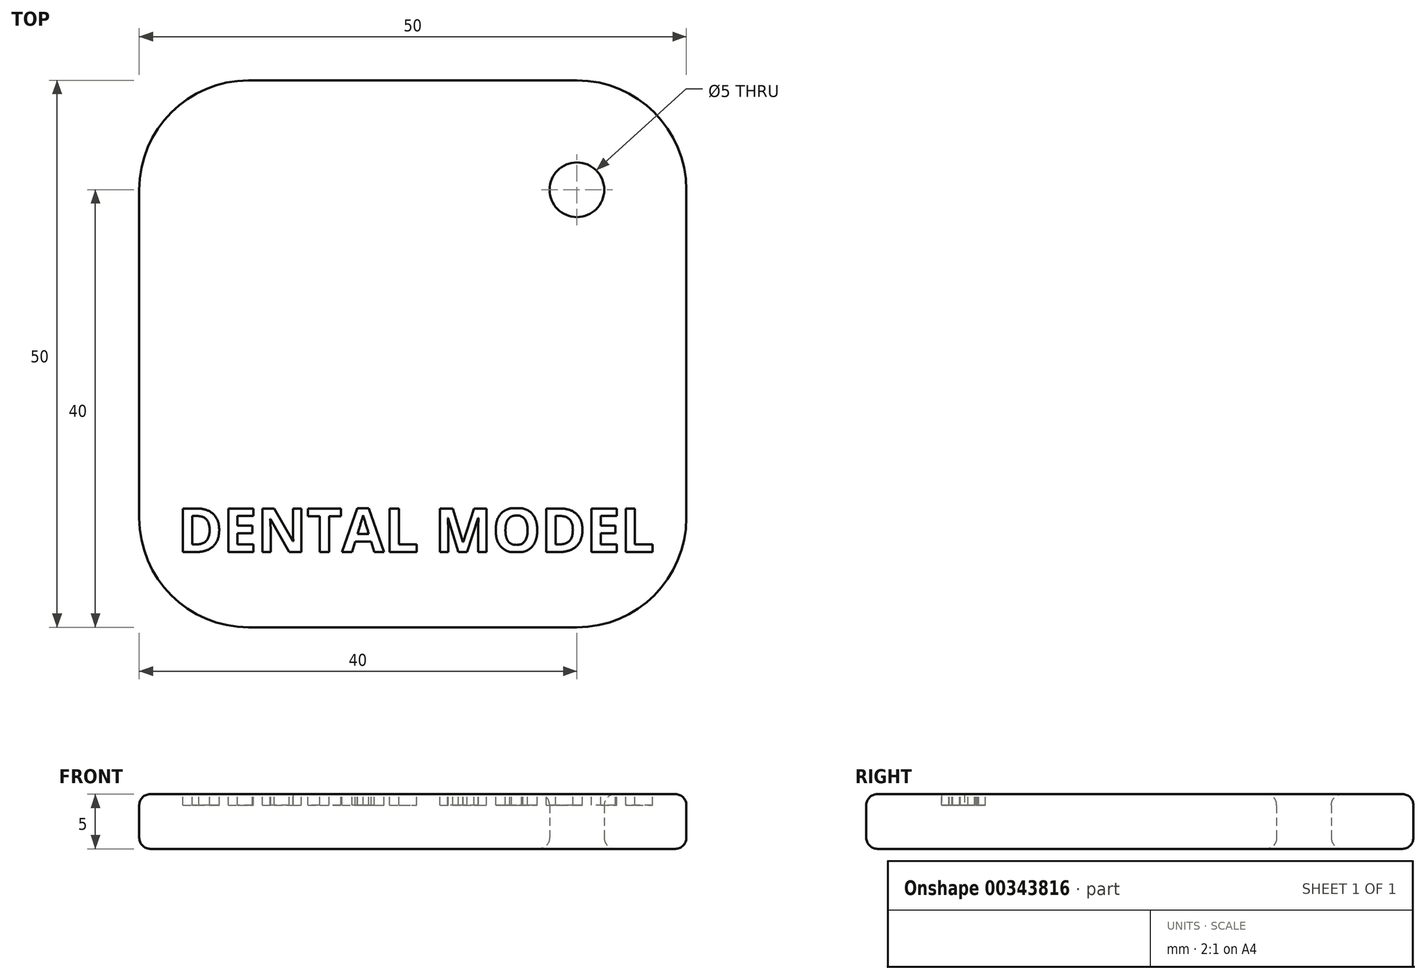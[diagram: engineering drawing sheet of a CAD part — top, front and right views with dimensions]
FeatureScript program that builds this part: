
annotation { "Feature Type Name" : "Feature", "Feature Type Description" : "" }
export const myFeature = defineFeature(function(context is Context, id is Id, definition is map)
    precondition{}
    {
        {
            var Q0;
            Q0=qCreatedBy(makeId("Top.planeOp"),FACE);
            var sketch = newSketch(context, id + "F0", { "sketchPlane" : qUnion([Q0])});
            skLineSegment(sketch, "E0.bottom", {"start": v(10, 0) * mm, "end": v(40, 0) * mm});
            skLineSegment(sketch, "E0.top", {"start": v(10, -50) * mm, "end": v(40, -50) * mm});
            skLineSegment(sketch, "E0.left", {"start": v(0, -10) * mm, "end": v(0, -40) * mm});
            skLineSegment(sketch, "E0.right", {"start": v(50, -10) * mm, "end": v(50, -40) * mm});
            skPoint(sketch, "E1.visualSharp", {"position": v(50, 0) * mm});
            skArc(sketch, "E1.filletArc", {"start": v(50, -10) * mm, "mid": v(47.07, -2.93) * mm, "end": v(40, 0) * mm});
            skPoint(sketch, "E2.visualSharp", {"position": v(50, -50) * mm});
            skArc(sketch, "E2.filletArc", {"start": v(40, -50) * mm, "mid": v(47.07, -47.07) * mm, "end": v(50, -40) * mm});
            skPoint(sketch, "E3.visualSharp", {"position": v(0, -50) * mm});
            skArc(sketch, "E3.filletArc", {"start": v(0, -40) * mm, "mid": v(2.93, -47.07) * mm, "end": v(10, -50) * mm});
            skPoint(sketch, "E4.visualSharp", {"position": v(0, 0) * mm});
            skArc(sketch, "E4.filletArc", {"start": v(10, 0) * mm, "mid": v(2.93, -2.93) * mm, "end": v(0, -10) * mm});
            skCircle(sketch, "E5", {"center": v(40, -10) * mm, "radius": 2.5 * mm});
            skSolve(sketch);
        }
        {
            var Q0;
            Q0=makeQuery(id+"F0.imprint","IMPRINT",FACE,{"disambiguationData":[TD([[makeQuery(id+"F0.imprint","IMPRINT",EDGE,{"derivedFrom":sQuery(id+"F0.wireOp",EDGE,"E0.bottom")}),-1.0]])]});
            extrude(context, id + "F1", {"entities" : qUnion([Q0]), "depth" : 5 * mm, "offsetDistance" : 25 * mm});
        }
        {
            var Q0;
            Q0=makeQuery(id+"F1.opExtrude","CAP_FACE",FACE,{"disambiguationData":[OSD([sQuery(id+"F0.wireOp",EDGE,"E0.bottom"),sQuery(id+"F0.wireOp",EDGE,"E0.top"),sQuery(id+"F0.wireOp",EDGE,"E0.left"),sQuery(id+"F0.wireOp",EDGE,"E0.right"),sQuery(id+"F0.wireOp",EDGE,"E1.filletArc"),sQuery(id+"F0.wireOp",EDGE,"E2.filletArc"),sQuery(id+"F0.wireOp",EDGE,"E3.filletArc"),sQuery(id+"F0.wireOp",EDGE,"E4.filletArc"),sQuery(id+"F0.wireOp",EDGE,"E5")])],"isStart":false});
            var Q1;
            Q1=makeQuery(id+"F1.opExtrude","CAP_FACE",FACE,{"disambiguationData":[OSD([sQuery(id+"F0.wireOp",EDGE,"E0.bottom"),sQuery(id+"F0.wireOp",EDGE,"E0.top"),sQuery(id+"F0.wireOp",EDGE,"E0.left"),sQuery(id+"F0.wireOp",EDGE,"E0.right"),sQuery(id+"F0.wireOp",EDGE,"E1.filletArc"),sQuery(id+"F0.wireOp",EDGE,"E2.filletArc"),sQuery(id+"F0.wireOp",EDGE,"E3.filletArc"),sQuery(id+"F0.wireOp",EDGE,"E4.filletArc"),sQuery(id+"F0.wireOp",EDGE,"E5")])],"isStart":true});
            fillet(context, id + "F2", {"entities" : qUnion([Q0, Q1]), "radius" : 1 * mm, "tangentPropagation" : true, "allowEdgeOverflow" : false});
        }
        {
            var Q0;
            Q0=makeQuery(id+"F1.opExtrude","CAP_FACE",FACE,{"disambiguationData":[OSD([sQuery(id+"F0.wireOp",EDGE,"E0.bottom"),sQuery(id+"F0.wireOp",EDGE,"E0.top"),sQuery(id+"F0.wireOp",EDGE,"E0.left"),sQuery(id+"F0.wireOp",EDGE,"E0.right"),sQuery(id+"F0.wireOp",EDGE,"E1.filletArc"),sQuery(id+"F0.wireOp",EDGE,"E2.filletArc"),sQuery(id+"F0.wireOp",EDGE,"E3.filletArc"),sQuery(id+"F0.wireOp",EDGE,"E4.filletArc"),sQuery(id+"F0.wireOp",EDGE,"E5")])],"isStart":false});
            var sketch = newSketch(context, id + "F3", { "sketchPlane" : qUnion([Q0])});
            skLineSegment(sketch, "E6", {"start": v(25, -49) * mm, "end": v(25, -1) * mm, "construction": true});
            skLineSegment(sketch, "E7.bottom", {"start": v(3.5, -39.1) * mm, "end": v(46.5, -39.1) * mm});
            skLineSegment(sketch, "E7.top", {"start": v(3.5, -43.1) * mm, "end": v(46.5, -43.1) * mm});
            skLineSegment(sketch, "E7.left", {"start": v(3.5, -39.1) * mm, "end": v(3.5, -43.1) * mm});
            skLineSegment(sketch, "E7.right", {"start": v(46.5, -39.1) * mm, "end": v(46.5, -43.1) * mm});
            skLineSegment(sketch, "E8.bottom", {"start": v(25, -43.1) * mm, "end": v(25, -43.1) * mm});
            skLineSegment(sketch, "E8.top", {"start": v(25, -43.1) * mm, "end": v(25, -43.1) * mm});
            skLineSegment(sketch, "E8.left", {"start": v(25, -43.1) * mm, "end": v(25, -43.1) * mm});
            skLineSegment(sketch, "E8.right", {"start": v(25, -43.1) * mm, "end": v(25, -43.1) * mm});
            skText(sketch, "E9", { "text": "DENTAL MODEL", "fontName": "OpenSans-Bold.ttf"});
            const initialGuessF3  = {"E9": [0.0035, -0.04312, 1, 0, 0.00402]};
            skSetInitialGuess(sketch, initialGuessF3);
            skSolve(sketch);
        }
        {
            var Q0;
            {var subQ6=sQuery(id+"F3.wireOp",EDGE,"E9.sketch_text.stroke-0");Q0=makeQuery(id+"F3.imprint","IMPRINT",FACE,{"disambiguationData":[TD([[makeQuery(id+"F3.imprint","IMPRINT",EDGE,{"derivedFrom":subQ6}),-1.0]])]});}
            var Q1;
            {var subQ5=sQuery(id+"F3.wireOp",EDGE,"E9.sketch_text.stroke-14");Q1=makeQuery(id+"F3.imprint","IMPRINT",FACE,{"disambiguationData":[TD([[makeQuery(id+"F3.imprint","IMPRINT",EDGE,{"derivedFrom":subQ5}),-1.0]])]});}
            var Q2;
            {var subQ11=sQuery(id+"F3.wireOp",EDGE,"E9.sketch_text.stroke-26");Q2=makeQuery(id+"F3.imprint","IMPRINT",FACE,{"disambiguationData":[TD([[makeQuery(id+"F3.imprint","IMPRINT",EDGE,{"derivedFrom":subQ11}),-1.0]])]});}
            var Q3;
            {var subQ0=sQuery(id+"F3.wireOp",EDGE,"E9.sketch_text.stroke-40");Q3=makeQuery(id+"F3.imprint","IMPRINT",FACE,{"disambiguationData":[TD([[makeQuery(id+"F3.imprint","IMPRINT",EDGE,{"derivedFrom":subQ0}),-1.0]])]});}
            var Q4;
            {var subQ7=sQuery(id+"F3.wireOp",EDGE,"E9.sketch_text.stroke-47");Q4=makeQuery(id+"F3.imprint","IMPRINT",FACE,{"disambiguationData":[TD([[makeQuery(id+"F3.imprint","IMPRINT",EDGE,{"derivedFrom":subQ7}),-1.0]])]});}
            var Q5;
            {var subQ0=sQuery(id+"F3.wireOp",EDGE,"E9.sketch_text.stroke-59");Q5=makeQuery(id+"F3.imprint","IMPRINT",FACE,{"disambiguationData":[TD([[makeQuery(id+"F3.imprint","IMPRINT",EDGE,{"derivedFrom":subQ0}),-1.0]])]});}
            var Q6;
            {var subQ7=sQuery(id+"F3.wireOp",EDGE,"E9.sketch_text.stroke-64");Q6=makeQuery(id+"F3.imprint","IMPRINT",FACE,{"disambiguationData":[TD([[makeQuery(id+"F3.imprint","IMPRINT",EDGE,{"derivedFrom":subQ7}),-1.0]])]});}
            var Q7;
            {var subQ8=sQuery(id+"F3.wireOp",EDGE,"E9.sketch_text.stroke-97");Q7=makeQuery(id+"F3.imprint","IMPRINT",FACE,{"disambiguationData":[TD([[makeQuery(id+"F3.imprint","IMPRINT",EDGE,{"derivedFrom":subQ8}),-1.0]])]});}
            var Q8;
            {var subQ5=sQuery(id+"F3.wireOp",EDGE,"E9.sketch_text.stroke-110");Q8=makeQuery(id+"F3.imprint","IMPRINT",FACE,{"disambiguationData":[TD([[makeQuery(id+"F3.imprint","IMPRINT",EDGE,{"derivedFrom":subQ5}),-1.0]])]});}
            var Q9;
            {var subQ8=sQuery(id+"F3.wireOp",EDGE,"E9.sketch_text.stroke-93");Q9=makeQuery(id+"F3.imprint","IMPRINT",FACE,{"disambiguationData":[TD([[makeQuery(id+"F3.imprint","IMPRINT",EDGE,{"derivedFrom":subQ8}),-1.0]])]});}
            var Q10;
            {var subQ0=sQuery(id+"F3.wireOp",EDGE,"E9.sketch_text.stroke-100");Q10=makeQuery(id+"F3.imprint","IMPRINT",FACE,{"disambiguationData":[TD([[makeQuery(id+"F3.imprint","IMPRINT",EDGE,{"derivedFrom":subQ0}),-1.0]])]});}
            var Q11;
            {var subQ7=sQuery(id+"F3.wireOp",EDGE,"E9.sketch_text.stroke-65");Q11=makeQuery(id+"F3.imprint","IMPRINT",FACE,{"disambiguationData":[TD([[makeQuery(id+"F3.imprint","IMPRINT",EDGE,{"derivedFrom":subQ7}),-1.0]])]});}
            var Q12;
            {var subQ0=sQuery(id+"F3.wireOp",EDGE,"E9.sketch_text.stroke-122");Q12=makeQuery(id+"F3.imprint","IMPRINT",FACE,{"disambiguationData":[TD([[makeQuery(id+"F3.imprint","IMPRINT",EDGE,{"derivedFrom":subQ0}),-1.0]])]});}
            var Q13;
            {var subQ5=sQuery(id+"F3.wireOp",EDGE,"E9.sketch_text.stroke-111");Q13=makeQuery(id+"F3.imprint","IMPRINT",FACE,{"disambiguationData":[TD([[makeQuery(id+"F3.imprint","IMPRINT",EDGE,{"derivedFrom":subQ5}),-1.0]])]});}
            var Q14;
            {var subQ5=sQuery(id+"F3.wireOp",EDGE,"E9.sketch_text.stroke-125");Q14=makeQuery(id+"F3.imprint","IMPRINT",FACE,{"disambiguationData":[TD([[makeQuery(id+"F3.imprint","IMPRINT",EDGE,{"derivedFrom":subQ5}),-1.0]])]});}
            extrude(context, id + "F4", {"entities" : qUnion([Q0, Q1, Q2, Q3, Q4, Q5, Q6, Q7, Q8, Q9, Q10, Q11, Q12, Q13, Q14]), "operationType" : NewBodyOperationType.REMOVE, "oppositeDirection" : true, "depth" : 1 * mm, "offsetDistance" : 25 * mm});
        }
    });
